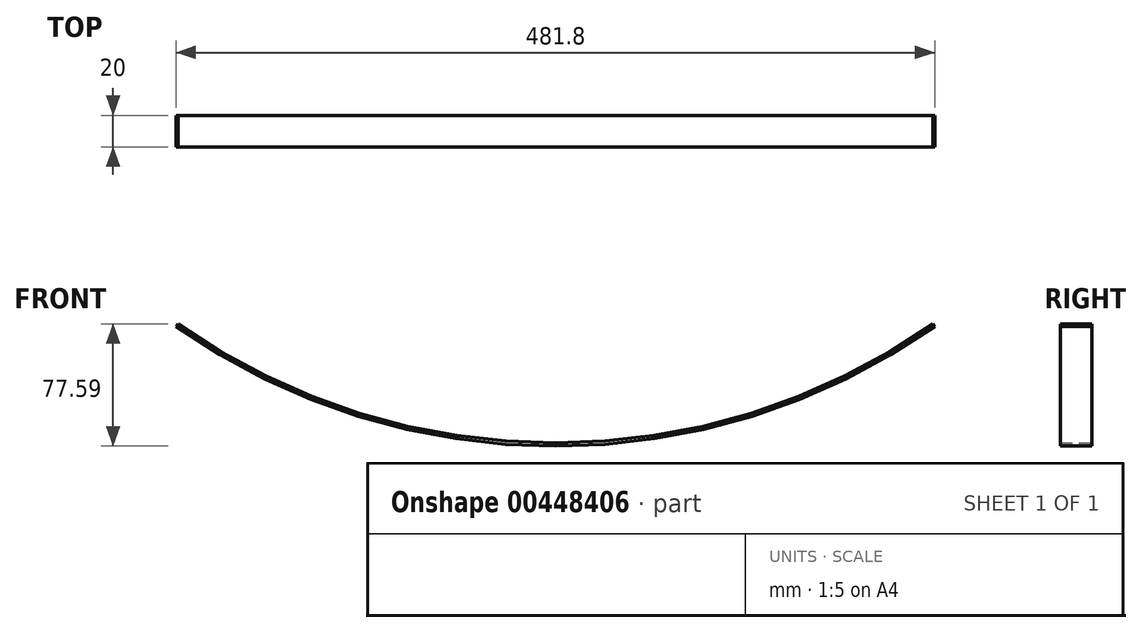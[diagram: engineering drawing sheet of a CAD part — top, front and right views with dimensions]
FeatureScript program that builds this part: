
annotation { "Feature Type Name" : "Feature", "Feature Type Description" : "" }
export const myFeature = defineFeature(function(context is Context, id is Id, definition is map)
    precondition{}
    {
        {
            var Q0;
            Q0=qCreatedBy(makeId("Front.planeOp"),FACE);
            var sketch = newSketch(context, id + "F0", { "sketchPlane" : qUnion([Q0])});
            skLineSegment(sketch, "E0", {"start": v(0, 0) * mm, "end": v(0, 420) * mm, "construction": true});
            skLineSegment(sketch, "E1", {"start": v(0, 420) * mm, "end": v(-240.9, 75.96) * mm, "construction": true});
            skArc(sketch, "E2", {"start": v(-240.9, 75.96) * mm, "mid": v(0, 0) * mm, "end": v(240.9, 75.96) * mm});
            skArc(sketch, "E3", {"start": v(-239.75, 77.6) * mm, "mid": v(0, 2) * mm, "end": v(239.75, 77.6) * mm});
            skLineSegment(sketch, "E4.MirrorCS", {"start": v(0, 420) * mm, "end": v(240.9, 75.96) * mm, "construction": true});
            skLineSegment(sketch, "E5", {"start": v(-240.9, 75.96) * mm, "end": v(-239.75, 77.6) * mm});
            skLineSegment(sketch, "E6", {"start": v(240.9, 75.96) * mm, "end": v(239.75, 77.6) * mm});
            skSolve(sketch);
        }
        {
            var Q0;
            Q0=qSketchRegion(id+"F0",true);
            extrude(context, id + "F1", {"entities" : qUnion([Q0]), "depth" : 20 * mm});
        }
    });
